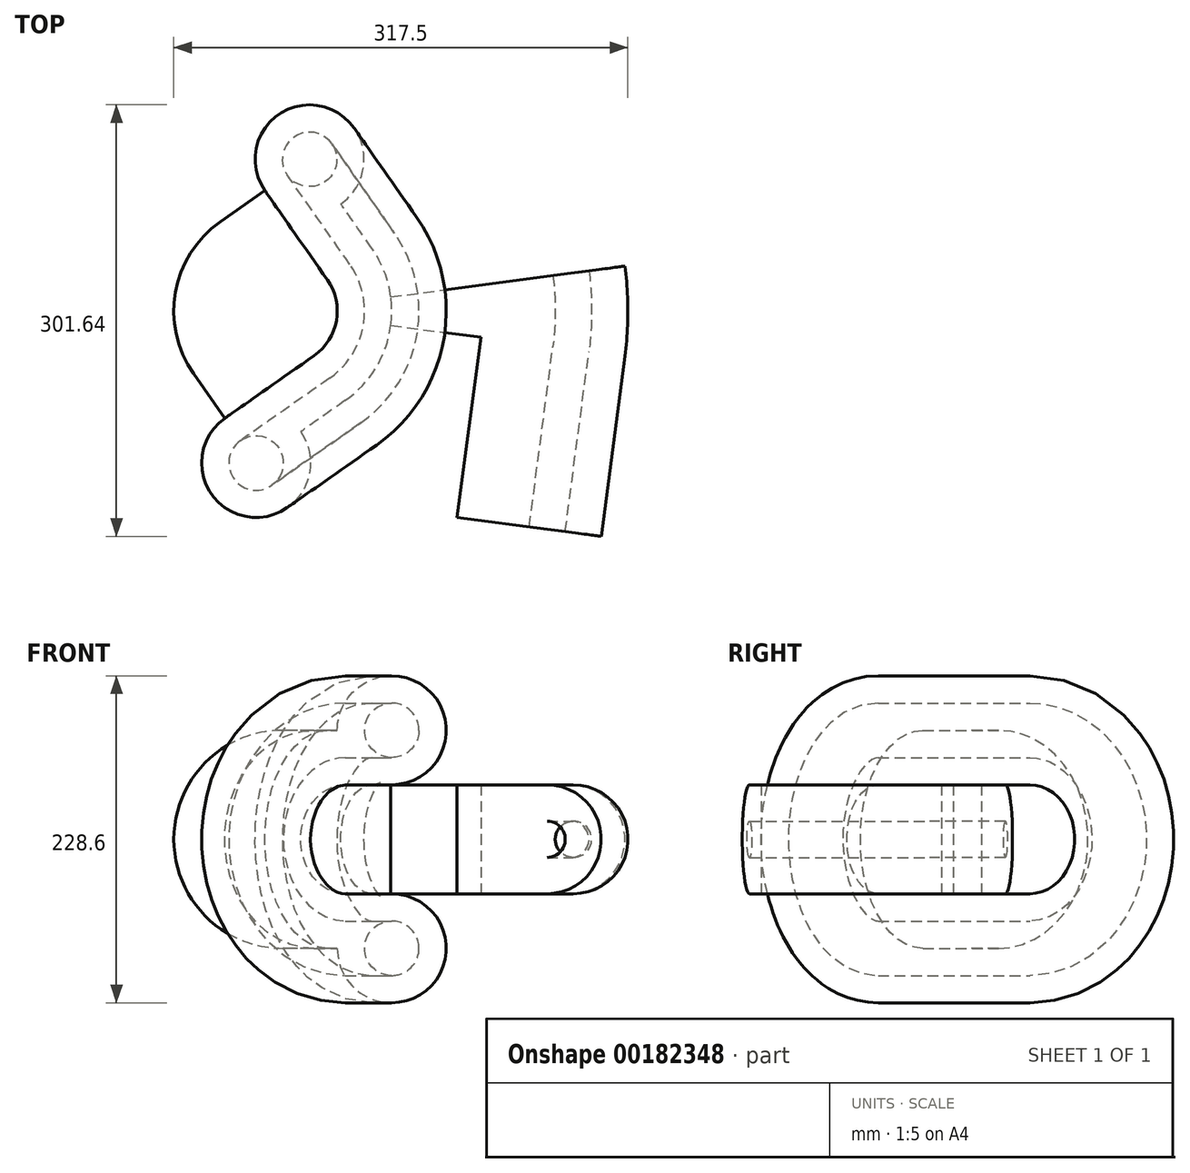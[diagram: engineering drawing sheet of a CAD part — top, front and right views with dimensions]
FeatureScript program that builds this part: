
annotation { "Feature Type Name" : "Feature", "Feature Type Description" : "" }
export const myFeature = defineFeature(function(context is Context, id is Id, definition is map)
    precondition{}
    {
        {
            var Q0;
            Q0=qCreatedBy(makeId("Front.planeOp"),FACE);
            var sketch = newSketch(context, id + "F0", { "sketchPlane" : qUnion([Q0])});
            skLineSegment(sketch, "E0.bottom", {"start": v(0, 38.1) * mm, "end": v(-38.1, 38.1) * mm});
            skLineSegment(sketch, "E0.top", {"start": v(38.1, -38.1) * mm, "end": v(-38.1, -38.1) * mm});
            skLineSegment(sketch, "E0.left", {"start": v(38.1, 0) * mm, "end": v(38.1, -38.1) * mm});
            skLineSegment(sketch, "E0.right", {"start": v(-38.1, 38.1) * mm, "end": v(-38.1, -38.1) * mm});
            skPoint(sketch, "E0.middle", {"position": v(0, 0) * mm});
            skArc(sketch, "E1", {"start": v(38.1, 0) * mm, "mid": v(65.04, 65.04) * mm, "end": v(0, 38.1) * mm});
            skSolve(sketch);
        }
        {
            var Q0;
            {var subQ0=sQuery(id+"F0.wireOp",EDGE,"E0.left");var subQ1=sQuery(id+"F0.wireOp",EDGE,"E0.bottom");var subQ2=makeQuery(id+"F0.imprint","INTERSECT",VERTEX,{"derivedFrom":[subQ1,subQ0]});Q0=makeQuery(id+"F0.imprint","IMPRINT",FACE,{"disambiguationData":[TD([[makeQuery(id+"F0.imprint","IMPRINT",EDGE,{"disambiguationData":[TD([[subQ2,-1.0]])],"derivedFrom":subQ1}),-1.0]])]});}
            var Q1;
            {var subQ0=sQuery(id+"F0.wireOp",EDGE,"E0.left");var subQ1=sQuery(id+"F0.wireOp",EDGE,"E0.bottom");var subQ2=makeQuery(id+"F0.imprint","INTERSECT",VERTEX,{"derivedFrom":[subQ1,subQ0]});Q1=makeQuery(id+"F0.imprint","IMPRINT",FACE,{"disambiguationData":[TD([[makeQuery(id+"F0.imprint","IMPRINT",EDGE,{"disambiguationData":[TD([[subQ2,-1.0]])],"derivedFrom":subQ1}),1.0]])]});}
            var Q2;
            Q2=sQuery(id+"F0.wireOp",EDGE,"E0.right");
            revolve(context, id + "F1", {"entities" : qUnion([Q0, Q1]), "axis" : qUnion([Q2]), "revolveType" : RevolveType.ONE_DIRECTION, "angle" : 55 * degree});
        }
        {
            var Q0;
            Q0=makeQuery(id+"F1.opRevolve","CAP_FACE",FACE,{"disambiguationData":[OSD([sQuery(id+"F0.wireOp",EDGE,"E0.bottom"),sQuery(id+"F0.wireOp",EDGE,"E0.top"),sQuery(id+"F0.wireOp",EDGE,"E0.left"),sQuery(id+"F0.wireOp",EDGE,"E0.right"),sQuery(id+"F0.wireOp",EDGE,"E1")])],"isStart":false});
            var sketch = newSketch(context, id + "F2", { "sketchPlane" : qUnion([Q0])});
            skCircle(sketch, "E2", {"center": v(54.35, 38.1) * mm, "radius": 19.05 * mm});
            skSolve(sketch);
        }
        {
            var Q0;
            Q0 = qSketchRegion(id + "F2", true);
            var Q1;
            Q1=makeQuery(id+"F1.opRevolve","CAP_EDGE",EDGE,{"disambiguationData":[OSD([sQuery(id+"F0.wireOp",EDGE,"E0.right")])],"isStart":true});
            revolve(context, id + "F3", {"operationType" : NewBodyOperationType.REMOVE, "entities" : qUnion([Q0]), "axis" : qUnion([Q1]), "revolveType" : RevolveType.ONE_DIRECTION, "oppositeDirection" : true, "angle" : 55 * degree});
        }
        {
            var Q0;
            Q0=makeQuery(id+"F1.opRevolve","CAP_FACE",FACE,{"disambiguationData":[OSD([sQuery(id+"F0.wireOp",EDGE,"E0.bottom"),sQuery(id+"F0.wireOp",EDGE,"E0.top"),sQuery(id+"F0.wireOp",EDGE,"E0.left"),sQuery(id+"F0.wireOp",EDGE,"E0.right"),sQuery(id+"F0.wireOp",EDGE,"E1")])],"isStart":false});
            var Q1;
            Q1=makeQuery(id+"F1.opRevolve","CAP_EDGE",EDGE,{"disambiguationData":[OSD([sQuery(id+"F0.wireOp",EDGE,"E0.top")])],"isStart":false});
            revolve(context, id + "F4", {"operationType" : NewBodyOperationType.ADD, "entities" : qUnion([Q0]), "axis" : qUnion([Q1]), "revolveType" : RevolveType.ONE_DIRECTION, "oppositeDirection" : true, "angle" : 90 * degree});
        }
        {
            var Q0;
            Q0=makeQuery(id+"F1.opRevolve","CAP_FACE",FACE,{"disambiguationData":[OSD([sQuery(id+"F0.wireOp",EDGE,"E0.bottom"),sQuery(id+"F0.wireOp",EDGE,"E0.top"),sQuery(id+"F0.wireOp",EDGE,"E0.left"),sQuery(id+"F0.wireOp",EDGE,"E0.right"),sQuery(id+"F0.wireOp",EDGE,"E1")])],"isStart":true});
            var Q1;
            {var subQ0=sQuery(id+"F0.wireOp",EDGE,"E0.right");Q1=makeQuery(id+"F4.boolean.opBoolean","MERGE",EDGE,{"derivedFrom":[makeQuery(id+"F1.opRevolve","CAP_EDGE",EDGE,{"disambiguationData":[OSD([subQ0])],"isStart":true}),makeQuery(id+"F4.opRevolve","CAP_EDGE",EDGE,{"disambiguationData":[OSD([subQ0])],"isStart":true})]});}
            revolve(context, id + "F5", {"operationType" : NewBodyOperationType.ADD, "entities" : qUnion([Q0]), "axis" : qUnion([Q1]), "revolveType" : RevolveType.ONE_DIRECTION, "oppositeDirection" : true, "angle" : 35 * degree});
        }
        {
            var Q0;
            {var subQ0=sQuery(id+"F0.wireOp",EDGE,"E0.right");Q0=makeQuery(id+"F5.boolean.opBoolean","MERGE",FACE,{"derivedFrom":[makeQuery(id+"F4.opRevolve","SWEPT_FACE",FACE,{"disambiguationData":[OSD([subQ0])]}),makeQuery(id+"F5.opRevolve","CAP_FACE",FACE,{"disambiguationData":[OSD([sQuery(id+"F0.wireOp",EDGE,"E0.bottom"),sQuery(id+"F0.wireOp",EDGE,"E0.top"),sQuery(id+"F0.wireOp",EDGE,"E0.left"),subQ0,sQuery(id+"F0.wireOp",EDGE,"E1")])],"isStart":false})]});}
            var Q1;
            Q1=makeQuery(id+"F5.boolean.opBoolean","MERGE",EDGE,{"derivedFrom":[makeQuery(id+"F4.opRevolve","CAP_EDGE",EDGE,{"disambiguationData":[OSD([sQuery(id+"F0.wireOp",EDGE,"E0.right")])],"isStart":false}),makeQuery(id+"F5.opRevolve","CAP_EDGE",EDGE,{"disambiguationData":[OSD([sQuery(id+"F0.wireOp",EDGE,"E0.top")])],"isStart":false})]});
            revolve(context, id + "F6", {"operationType" : NewBodyOperationType.ADD, "entities" : qUnion([Q0]), "axis" : qUnion([Q1]), "revolveType" : RevolveType.ONE_DIRECTION, "oppositeDirection" : true, "angle" : 90 * degree});
        }
        {
            var Q0;
            Q0=makeQuery(id+"F1.opRevolve","SWEPT_BODY",BODY,{"disambiguationData":[OSD([sQuery(id+"F0.wireOp",EDGE,"E0.bottom"),sQuery(id+"F0.wireOp",EDGE,"E0.top"),sQuery(id+"F0.wireOp",EDGE,"E0.left"),sQuery(id+"F0.wireOp",EDGE,"E0.right"),sQuery(id+"F0.wireOp",EDGE,"E1")])]});
            var Q1;
            {var subQ0=sQuery(id+"F0.wireOp",EDGE,"E1");var subQ1=sQuery(id+"F0.wireOp",EDGE,"E0.right");var subQ2=sQuery(id+"F0.wireOp",EDGE,"E0.left");var subQ3=sQuery(id+"F0.wireOp",EDGE,"E0.top");var subQ4=sQuery(id+"F0.wireOp",EDGE,"E0.bottom");Q1=makeQuery(id+"F6.boolean.opBoolean","MERGE",FACE,{"derivedFrom":[makeQuery(id+"F5.boolean.opBoolean","MERGE",FACE,{"derivedFrom":[makeQuery(id+"F4.boolean.opBoolean","MERGE",FACE,{"derivedFrom":[makeQuery(id+"F1.opRevolve","SWEPT_FACE",FACE,{"disambiguationData":[OSD([subQ3])]}),makeQuery(id+"F4.opRevolve","CAP_FACE",FACE,{"disambiguationData":[OSD([subQ4,subQ3,subQ2,subQ1,subQ0])],"isStart":false})]}),makeQuery(id+"F5.opRevolve","SWEPT_FACE",FACE,{"disambiguationData":[OSD([subQ3])]})]}),makeQuery(id+"F6.opRevolve","CAP_FACE",FACE,{"disambiguationData":[OSD([subQ4,subQ3,subQ2,subQ1,subQ0])],"isStart":false})]});}
            mirror(context, id + "F7", {"operationType" : NewBodyOperationType.ADD, "entities" : qUnion([Q0]), "mirrorPlane" : qUnion([Q1])});
        }
        {
            var Q0;
            Q0=qCreatedBy(makeId("Front.planeOp"),FACE);
            var sketch = newSketch(context, id + "F8", { "sketchPlane" : qUnion([Q0])});
            skLineSegment(sketch, "E3", {"start": v(38.1, 0) * mm, "end": v(38.1, -76.2) * mm});
            skLineSegment(sketch, "E4.bottom", {"start": v(38.1, 0) * mm, "end": v(165.1, 0) * mm});
            skLineSegment(sketch, "E4.top", {"start": v(38.1, -76.2) * mm, "end": v(165.1, -76.2) * mm});
            skArc(sketch, "E5", {"start": v(165.1, -76.2) * mm, "mid": v(203.2, -38.1) * mm, "end": v(165.1, 0) * mm});
            skCircle(sketch, "E6", {"center": v(165.1, -38.1) * mm, "radius": 12.7 * mm});
            skSolve(sketch);
        }
        {
            var Q0;
            Q0=makeQuery(id+"F8.imprint","IMPRINT",FACE,{"disambiguationData":[TD([[makeQuery(id+"F8.imprint","IMPRINT",EDGE,{"derivedFrom":sQuery(id+"F8.wireOp",EDGE,"E4.bottom")}),-1.0]])]});
            var Q1;
            {var subQ0=sQuery(id+"F0.wireOp",EDGE,"E0.left");var subQ1=makeQuery(id+"F5.boolean.opBoolean","MERGE",FACE,{"derivedFrom":[makeQuery(id+"F1.opRevolve","SWEPT_FACE",FACE,{"disambiguationData":[OSD([subQ0])]}),makeQuery(id+"F5.opRevolve","SWEPT_FACE",FACE,{"disambiguationData":[OSD([subQ0])]})]});Q1=makeQuery(id+"F7.boolean.opBoolean","MERGE",FACE,{"derivedFrom":[subQ1,makeQuery(id+"F7.opPattern","COPY",FACE,{"derivedFrom":subQ1,"instanceName":"1"})]});}
            revolve(context, id + "F9", {"operationType" : NewBodyOperationType.ADD, "entities" : qUnion([Q0]), "axis" : qUnion([Q1]), "revolveType" : RevolveType.SYMMETRIC, "angle" : 15 * degree});
        }
        {
            var Q0;
            Q0=makeQuery(id+"F9.opRevolve","CAP_FACE",FACE,{"disambiguationData":[OSD([sQuery(id+"F8.wireOp",EDGE,"E4.bottom"),sQuery(id+"F8.wireOp",EDGE,"E4.top"),sQuery(id+"F8.wireOp",EDGE,"E3"),sQuery(id+"F8.wireOp",EDGE,"E5"),sQuery(id+"F8.wireOp",EDGE,"E6")])],"isStart":true});
            var sketch = newSketch(context, id + "F10", { "sketchPlane" : qUnion([Q0])});
            skArc(sketch, "E7", {"start": v(165.43, -76.2) * mm, "mid": v(203.53, -38.1) * mm, "end": v(165.43, 0) * mm});
            skCircle(sketch, "E8", {"center": v(165.43, -38.1) * mm, "radius": 12.7 * mm});
            skLineSegment(sketch, "E9", {"start": v(165.43, 0) * mm, "end": v(101.93, 0) * mm});
            skLineSegment(sketch, "E10", {"start": v(101.93, 0) * mm, "end": v(101.93, -76.2) * mm});
            skLineSegment(sketch, "E11", {"start": v(101.93, -76.2) * mm, "end": v(165.43, -76.2) * mm});
            skSolve(sketch);
        }
        {
            var Q0;
            Q0=makeQuery(id+"F10.imprint","IMPRINT",FACE,{"disambiguationData":[TD([[makeQuery(id+"F10.imprint","IMPRINT",EDGE,{"derivedFrom":sQuery(id+"F10.wireOp",EDGE,"E7")}),1.0]])]});
            extrude(context, id + "F11", {"entities" : qUnion([Q0]), "operationType" : NewBodyOperationType.ADD, "depth" : 127 * mm});
        }
    });
